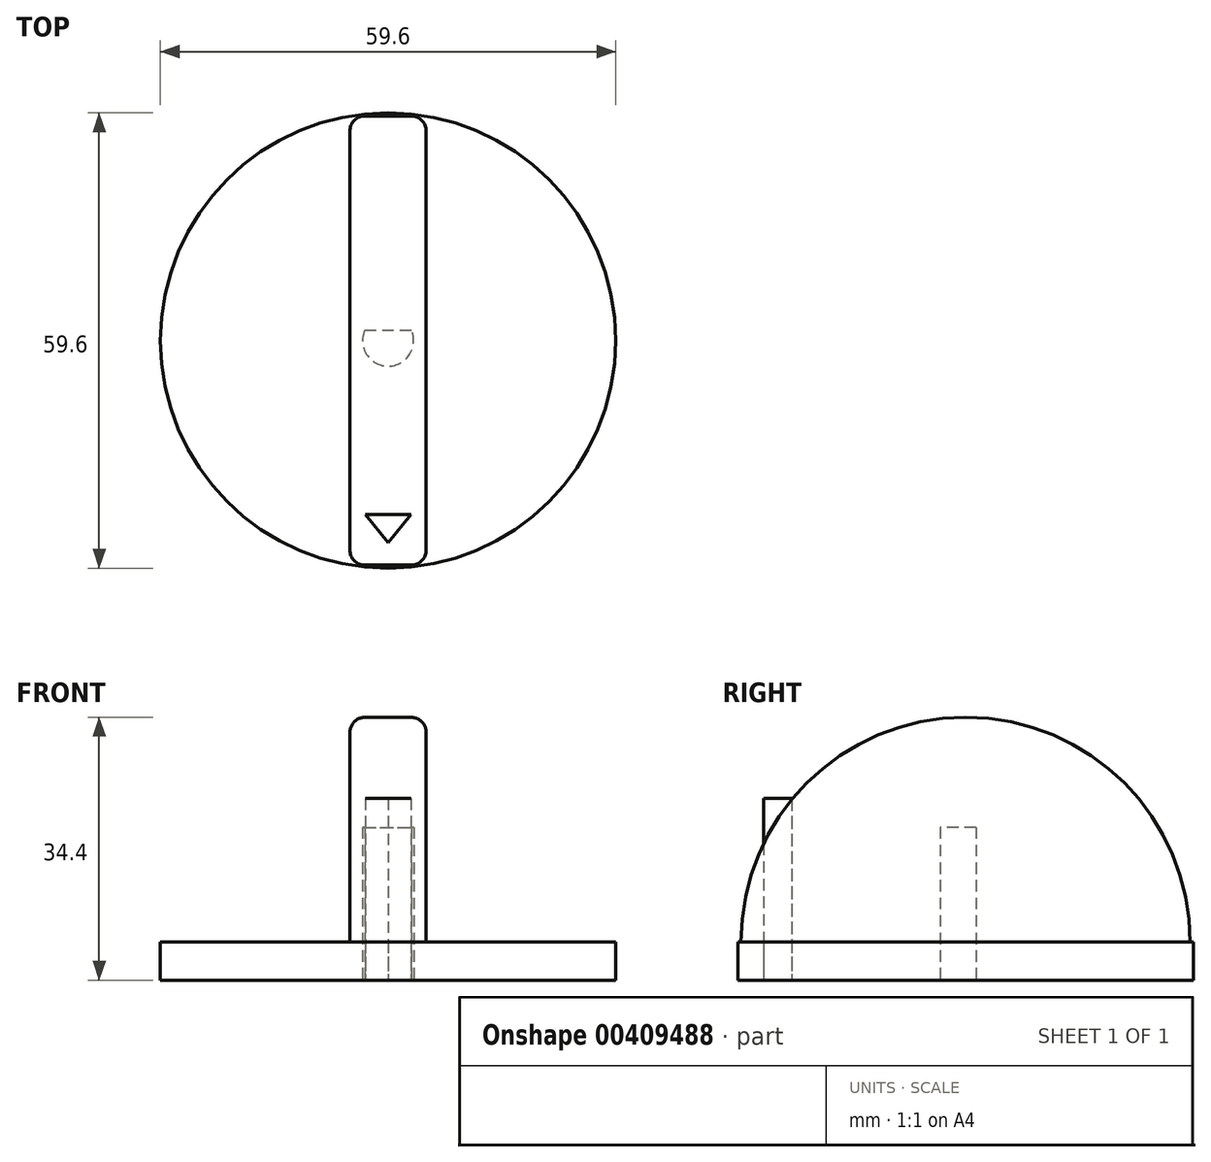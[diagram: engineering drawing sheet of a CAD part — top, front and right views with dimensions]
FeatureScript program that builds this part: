
annotation { "Feature Type Name" : "Feature", "Feature Type Description" : "" }
export const myFeature = defineFeature(function(context is Context, id is Id, definition is map)
    precondition{}
    {
        {
            var Q0;
            Q0=qCreatedBy(makeId("Top.planeOp"),FACE);
            var sketch = newSketch(context, id + "F0", { "sketchPlane" : qUnion([Q0])});
            skCircle(sketch, "E0", {"center": v(0, 0) * mm, "radius": 29.8 * mm});
            skLineSegment(sketch, "E1", {"start": v(-3, -22.76) * mm, "end": v(0, -26.45) * mm});
            skLineSegment(sketch, "E2", {"start": v(-3, -22.76) * mm, "end": v(0, -22.76) * mm});
            skLineSegment(sketch, "E3.MirrorCS", {"start": v(3, -22.76) * mm, "end": v(0, -26.45) * mm});
            skLineSegment(sketch, "E4.MirrorCS", {"start": v(0, -22.76) * mm, "end": v(3, -22.76) * mm});
            skSolve(sketch);
        }
        {
            var Q0;
            Q0=makeQuery(id+"F0.imprint","IMPRINT",FACE,{"disambiguationData":[TD([[makeQuery(id+"F0.imprint","IMPRINT",EDGE,{"derivedFrom":sQuery(id+"F0.wireOp",EDGE,"E0")}),1.0]])]});
            extrude(context, id + "F1", {"entities" : qUnion([Q0]), "depth" : 5 * mm});
        }
        {
            var Q0;
            Q0=qCreatedBy(makeId("Right.planeOp"),FACE);
            var sketch = newSketch(context, id + "F2", { "sketchPlane" : qUnion([Q0])});
            skLineSegment(sketch, "E5", {"start": v(29.4, 5) * mm, "end": v(-29.4, 5) * mm});
            skArc(sketch, "E6", {"start": v(-29.4, 5) * mm, "mid": v(0, 34.4) * mm, "end": v(29.4, 5) * mm});
            skSolve(sketch);
        }
        {
            var Q0;
            Q0=makeQuery(id+"F2.imprint","IMPRINT",FACE,{"disambiguationData":[TD([[makeQuery(id+"F2.imprint","IMPRINT",EDGE,{"derivedFrom":sQuery(id+"F2.wireOp",EDGE,"E5")}),-1.0]])]});
            extrude(context, id + "F3", {"entities" : qUnion([Q0]), "operationType" : NewBodyOperationType.ADD, "oppositeDirection" : true, "depth" : 5 * mm, "hasSecondDirection" : true, "secondDirectionOppositeDirection" : false, "secondDirectionDepth" : 5 * mm});
        }
        {
            var Q0;
            Q0=qCreatedBy(makeId("Top.planeOp"),FACE);
            var sketch = newSketch(context, id + "F4", { "sketchPlane" : qUnion([Q0])});
            skCircle(sketch, "E7", {"center": v(0, 0) * mm, "radius": 3.35 * mm});
            skLineSegment(sketch, "E8", {"start": v(-3.05, 1.38) * mm, "end": v(3.05, 1.38) * mm});
            skLineSegment(sketch, "E9", {"start": v(0, 0) * mm, "end": v(0, -3.35) * mm, "construction": true});
            skSolve(sketch);
        }
        {
            var Q0;
            {var subQ0=sQuery(id+"F4.wireOp",EDGE,"E8");Q0=makeQuery(id+"F4.imprint","IMPRINT",FACE,{"disambiguationData":[TD([[makeQuery(id+"F4.imprint","IMPRINT",EDGE,{"derivedFrom":subQ0}),-1.0]])]});}
            extrude(context, id + "F5", {"entities" : qUnion([Q0]), "operationType" : NewBodyOperationType.REMOVE, "depth" : 20 * mm});
        }
        {
            var Q0;
            Q0=makeQuery(id+"F0.imprint","IMPRINT",FACE,{"disambiguationData":[TD([[makeQuery(id+"F0.imprint","IMPRINT",EDGE,{"derivedFrom":sQuery(id+"F0.wireOp",EDGE,"E1")}),1.0]])]});
            extrude(context, id + "F6", {"entities" : qUnion([Q0]), "depth" : 23.78 * mm});
        }
        {
            var Q0;
            Q0=makeQuery(id+"F3.opExtrude","CAP_EDGE",EDGE,{"disambiguationData":[OSD([sQuery(id+"F2.wireOp",EDGE,"E6")])],"isStart":false});
            var Q1;
            Q1=makeQuery(id+"F3.opExtrude","CAP_EDGE",EDGE,{"disambiguationData":[OSD([sQuery(id+"F2.wireOp",EDGE,"E6")])],"isStart":true});
            fillet(context, id + "F7", {"entities" : qUnion([Q0, Q1]), "radius" : 2 * mm, "tangentPropagation" : true, "allowEdgeOverflow" : false});
        }
    });
